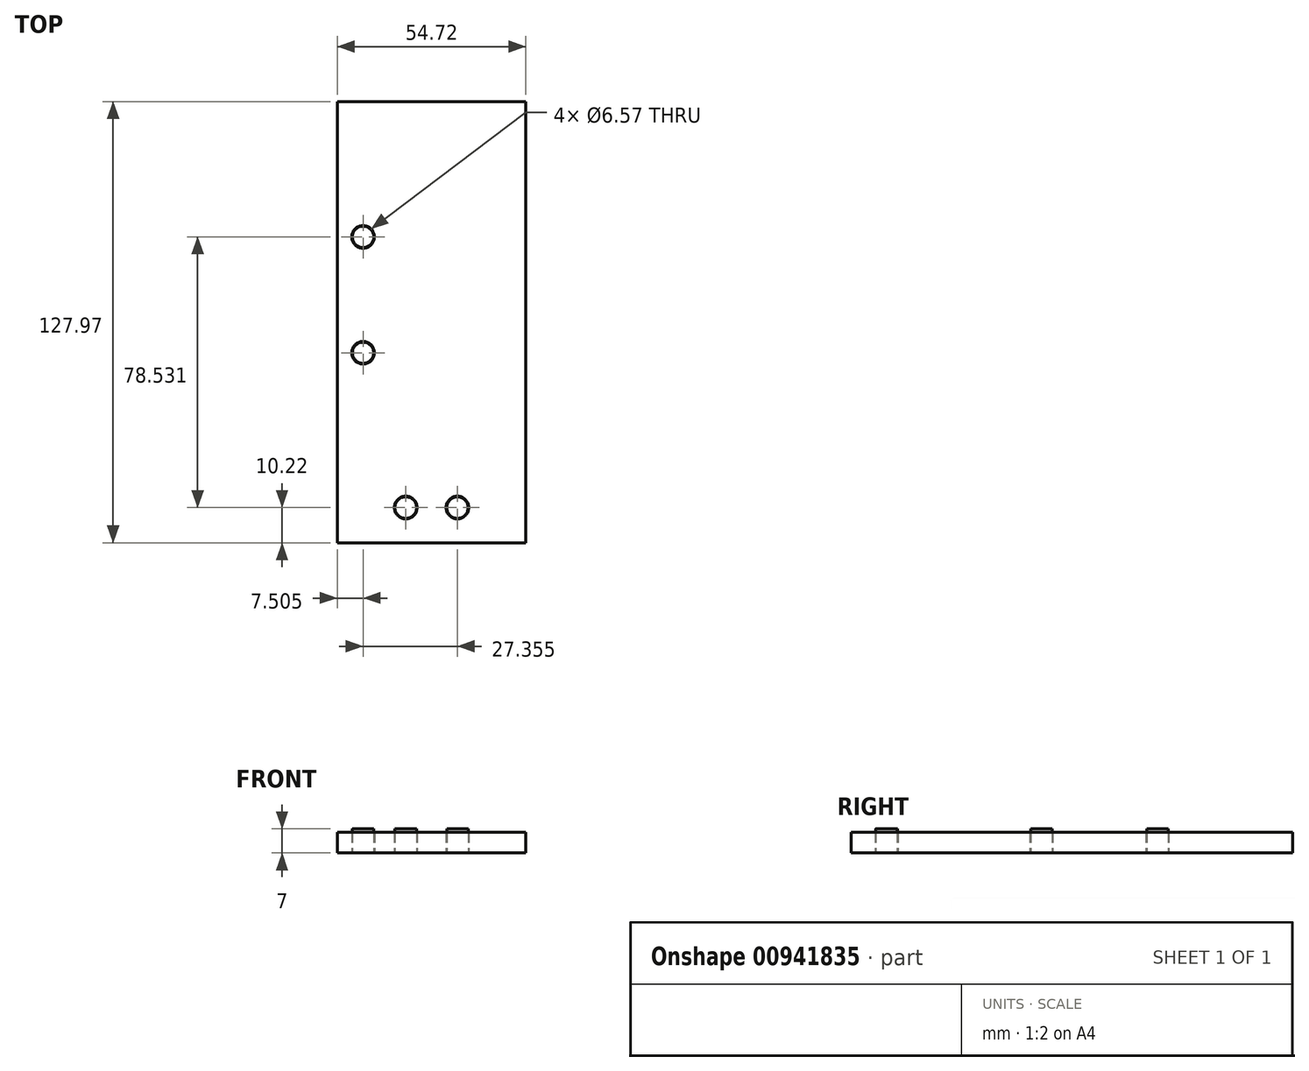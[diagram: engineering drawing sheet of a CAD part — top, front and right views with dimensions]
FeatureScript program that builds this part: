
annotation { "Feature Type Name" : "Feature", "Feature Type Description" : "" }
export const myFeature = defineFeature(function(context is Context, id is Id, definition is map)
    precondition{}
    {
        {
            var Q0;
            Q0=qCreatedBy(makeId("Top.planeOp"),FACE);
            var sketch = newSketch(context, id + "F0", { "sketchPlane" : qUnion([Q0])});
            skLineSegment(sketch, "E0.bottom", {"start": v(27.36, -10.22) * mm, "end": v(-27.36, -10.22) * mm});
            skLineSegment(sketch, "E0.top", {"start": v(27.36, 10.22) * mm, "end": v(-27.36, 10.22) * mm});
            skLineSegment(sketch, "E0.left", {"start": v(27.36, -10.22) * mm, "end": v(27.36, 10.22) * mm});
            skLineSegment(sketch, "E0.right", {"start": v(-27.36, -10.22) * mm, "end": v(-27.36, 10.22) * mm});
            skPoint(sketch, "E0.middle", {"position": v(0, 0) * mm});
            skLineSegment(sketch, "E1", {"start": v(27.36, 10.22) * mm, "end": v(27.36, 117.75) * mm});
            skLineSegment(sketch, "E2", {"start": v(-27.36, 10.22) * mm, "end": v(-27.36, 117.75) * mm});
            skLineSegment(sketch, "E3", {"start": v(-27.36, 117.75) * mm, "end": v(27.36, 117.75) * mm});
            skCircle(sketch, "E4", {"center": v(7.5, 0) * mm, "radius": 3.28 * mm});
            skCircle(sketch, "E5", {"center": v(-7.47, 0) * mm, "radius": 3.28 * mm});
            skCircle(sketch, "E6", {"center": v(-19.85, 78.53) * mm, "radius": 3.28 * mm});
            skCircle(sketch, "E7", {"center": v(-19.85, 44.9) * mm, "radius": 3.28 * mm});
            skCircle(sketch, "E8", {"center": v(-19.85, 78.53) * mm, "radius": 3.1 * mm});
            skCircle(sketch, "E9", {"center": v(-19.85, 44.9) * mm, "radius": 3.08 * mm});
            skCircle(sketch, "E10", {"center": v(-7.47, 0) * mm, "radius": 3.15 * mm});
            skCircle(sketch, "E11", {"center": v(7.5, 0) * mm, "radius": 3.1 * mm});
            skSolve(sketch);
        }
        {
            var Q0;
            Q0=makeQuery(id+"F0.imprint","IMPRINT",FACE,{"disambiguationData":[TD([[makeQuery(id+"F0.imprint","IMPRINT",EDGE,{"derivedFrom":sQuery(id+"F0.wireOp",EDGE,"E0.bottom")}),-1.0]])]});
            var Q1;
            Q1=makeQuery(id+"F0.imprint","IMPRINT",FACE,{"disambiguationData":[TD([[makeQuery(id+"F0.imprint","IMPRINT",EDGE,{"derivedFrom":sQuery(id+"F0.wireOp",EDGE,"E0.top")}),-1.0]])]});
            extrude(context, id + "F1", {"entities" : qUnion([Q0, Q1]), "depth" : 6 * mm, "offsetDistance" : 25 * mm});
        }
        {
            var Q0;
            Q0=makeQuery(id+"F0.imprint","IMPRINT",FACE,{"disambiguationData":[TD([[makeQuery(id+"F0.imprint","IMPRINT",EDGE,{"derivedFrom":sQuery(id+"F0.wireOp",EDGE,"E10")}),1.0]])]});
            var Q1;
            Q1=makeQuery(id+"F0.imprint","IMPRINT",FACE,{"disambiguationData":[TD([[makeQuery(id+"F0.imprint","IMPRINT",EDGE,{"derivedFrom":sQuery(id+"F0.wireOp",EDGE,"E11")}),1.0]])]});
            var Q2;
            Q2=makeQuery(id+"F0.imprint","IMPRINT",FACE,{"disambiguationData":[TD([[makeQuery(id+"F0.imprint","IMPRINT",EDGE,{"derivedFrom":sQuery(id+"F0.wireOp",EDGE,"E9")}),1.0]])]});
            var Q3;
            Q3=makeQuery(id+"F0.imprint","IMPRINT",FACE,{"disambiguationData":[TD([[makeQuery(id+"F0.imprint","IMPRINT",EDGE,{"derivedFrom":sQuery(id+"F0.wireOp",EDGE,"E8")}),1.0]])]});
            extrude(context, id + "F2", {"entities" : qUnion([Q0, Q1, Q2, Q3]), "depth" : 7 * mm, "offsetDistance" : 25 * mm});
        }
        {
            var Q0;
            Q0=makeQuery(id+"F2.opExtrude","SWEPT_BODY",BODY,{"disambiguationData":[OSD([sQuery(id+"F0.wireOp",EDGE,"E8")])]});
            var Q1;
            Q1=makeQuery(id+"F2.opExtrude","SWEPT_BODY",BODY,{"disambiguationData":[OSD([sQuery(id+"F0.wireOp",EDGE,"E9")])]});
            var Q2;
            Q2=makeQuery(id+"F2.opExtrude","SWEPT_BODY",BODY,{"disambiguationData":[OSD([sQuery(id+"F0.wireOp",EDGE,"E10")])]});
            var Q3;
            Q3=makeQuery(id+"F2.opExtrude","SWEPT_BODY",BODY,{"disambiguationData":[OSD([sQuery(id+"F0.wireOp",EDGE,"E11")])]});
            var Q4;
            Q4=makeQuery(id+"F1.opExtrude","SWEPT_BODY",BODY,{"disambiguationData":[OSD([sQuery(id+"F0.wireOp",EDGE,"E0.bottom"),sQuery(id+"F0.wireOp",EDGE,"E0.left"),sQuery(id+"F0.wireOp",EDGE,"E0.right"),sQuery(id+"F0.wireOp",EDGE,"E1"),sQuery(id+"F0.wireOp",EDGE,"E2"),sQuery(id+"F0.wireOp",EDGE,"E3"),sQuery(id+"F0.wireOp",EDGE,"E4"),sQuery(id+"F0.wireOp",EDGE,"E5"),sQuery(id+"F0.wireOp",EDGE,"E6"),sQuery(id+"F0.wireOp",EDGE,"E7")])]});
            transform(context, id + "F3", {"entities" : qUnion([Q0, Q1, Q2, Q3, Q4]), "transformType" : TransformType.TRANSLATION_3D, "dx" : 0 * mm, "dy" : 0 * mm, "dz" : 10 * mm, "makeCopy" : false});
        }
    });
